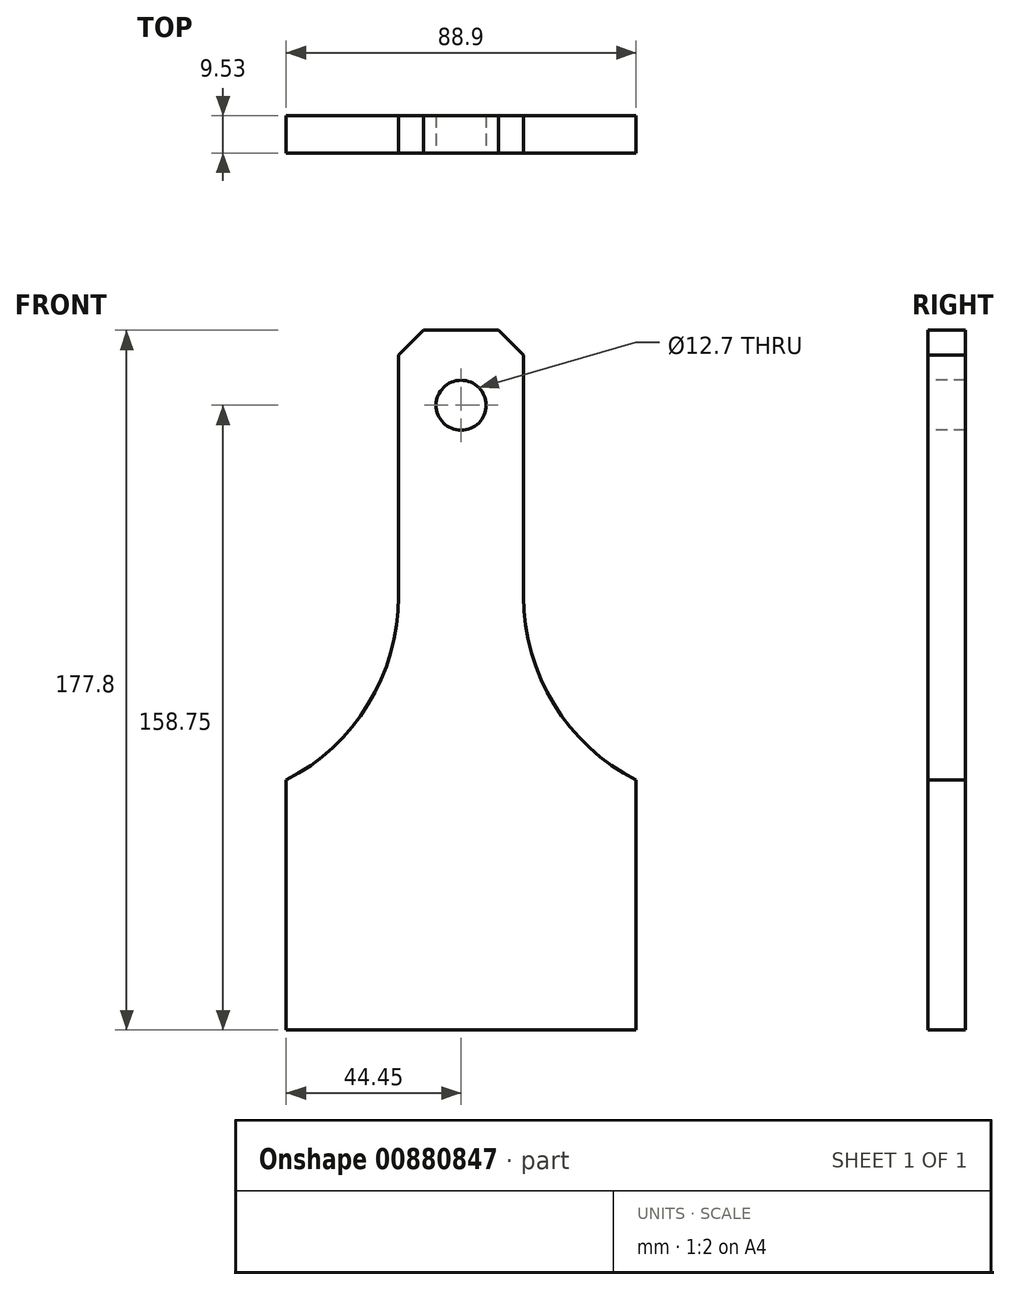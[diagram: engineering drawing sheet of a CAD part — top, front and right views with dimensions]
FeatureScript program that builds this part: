
annotation { "Feature Type Name" : "Feature", "Feature Type Description" : "" }
export const myFeature = defineFeature(function(context is Context, id is Id, definition is map)
    precondition{}
    {
        {
            var Q0;
            Q0=qCreatedBy(makeId("Front.planeOp"),FACE);
            var sketch = newSketch(context, id + "F0", { "sketchPlane" : qUnion([Q0])});
            skLineSegment(sketch, "E0.bottom", {"start": v(-44.45, 0) * mm, "end": v(44.45, 0) * mm});
            skLineSegment(sketch, "E0.top", {"start": v(-15.87, 177.8) * mm, "end": v(15.88, 177.8) * mm});
            skLineSegment(sketch, "E0.left", {"start": v(-44.45, 0) * mm, "end": v(-44.45, 63.5) * mm});
            skLineSegment(sketch, "E0.right", {"start": v(44.45, 0) * mm, "end": v(44.45, 63.5) * mm});
            skLineSegment(sketch, "E1", {"start": v(-15.87, 177.8) * mm, "end": v(-15.88, 110.16) * mm});
            skLineSegment(sketch, "E2", {"start": v(15.88, 177.8) * mm, "end": v(15.87, 110.16) * mm});
            skArc(sketch, "E3", {"start": v(15.88, 110.16) * mm, "mid": v(23.59, 82.8) * mm, "end": v(44.45, 63.5) * mm});
            skArc(sketch, "E4", {"start": v(-15.88, 110.16) * mm, "mid": v(-23.59, 82.8) * mm, "end": v(-44.45, 63.5) * mm});
            skSolve(sketch);
        }
        {
            var Q0;
            Q0 = qSketchRegion(id + "F0", true);
            extrude(context, id + "F1", {"entities" : qUnion([Q0]), "oppositeDirection" : true, "depth" : 9.52 * mm, "offsetDistance" : 25.4 * mm});
        }
        {
            var Q0;
            Q0 = qSketchRegion(id + "F0", true);
            extrude(context, id + "F2", {"entities" : qUnion([Q0]), "operationType" : NewBodyOperationType.ADD, "oppositeDirection" : true, "depth" : 6.35 * mm, "offsetDistance" : 25.4 * mm});
        }
        {
            var Q0;
            Q0=makeQuery(id+"F1.opExtrude","CAP_FACE",FACE,{"disambiguationData":[OSD([sQuery(id+"F0.wireOp",EDGE,"E0.bottom"),sQuery(id+"F0.wireOp",EDGE,"E0.top"),sQuery(id+"F0.wireOp",EDGE,"E0.left"),sQuery(id+"F0.wireOp",EDGE,"E0.right"),sQuery(id+"F0.wireOp",EDGE,"E1"),sQuery(id+"F0.wireOp",EDGE,"E2"),sQuery(id+"F0.wireOp",EDGE,"E3"),sQuery(id+"F0.wireOp",EDGE,"E4")])],"isStart":true});
            var sketch = newSketch(context, id + "F3", { "sketchPlane" : qUnion([Q0])});
            skCircle(sketch, "E5", {"center": v(0, 158.75) * mm, "radius": 6.35 * mm});
            skPoint(sketch, "E5.centerSnap0", {"position": v(0, 177.8) * mm});
            skSolve(sketch);
        }
        {
            var Q0;
            Q0=makeQuery(id+"F3.imprint","IMPRINT",FACE,{"disambiguationData":[TD([[makeQuery(id+"F3.imprint","IMPRINT",EDGE,{"derivedFrom":sQuery(id+"F3.wireOp",EDGE,"E5")}),1.0]])]});
            extrude(context, id + "F4", {"entities" : qUnion([Q0]), "operationType" : NewBodyOperationType.REMOVE, "endBound" : BoundingType.THROUGH_ALL, "oppositeDirection" : true, "depth" : 25.4 * mm, "offsetDistance" : 25.4 * mm});
        }
        {
            var Q0;
            Q0=makeQuery(id+"F1.opExtrude","SWEPT_EDGE",EDGE,{"disambiguationData":[OSD([sQuery(id+"F0.wireOp",EDGE,"E0.top"),sQuery(id+"F0.wireOp",EDGE,"E2")])]});
            var Q1;
            Q1=makeQuery(id+"F1.opExtrude","SWEPT_EDGE",EDGE,{"disambiguationData":[OSD([sQuery(id+"F0.wireOp",EDGE,"E0.top"),sQuery(id+"F0.wireOp",EDGE,"E1")])]});
            chamfer(context, id + "F5", {"entities" : qUnion([Q0, Q1]), "width" : 6.35 * mm, "tangentPropagation" : true});
        }
    });
